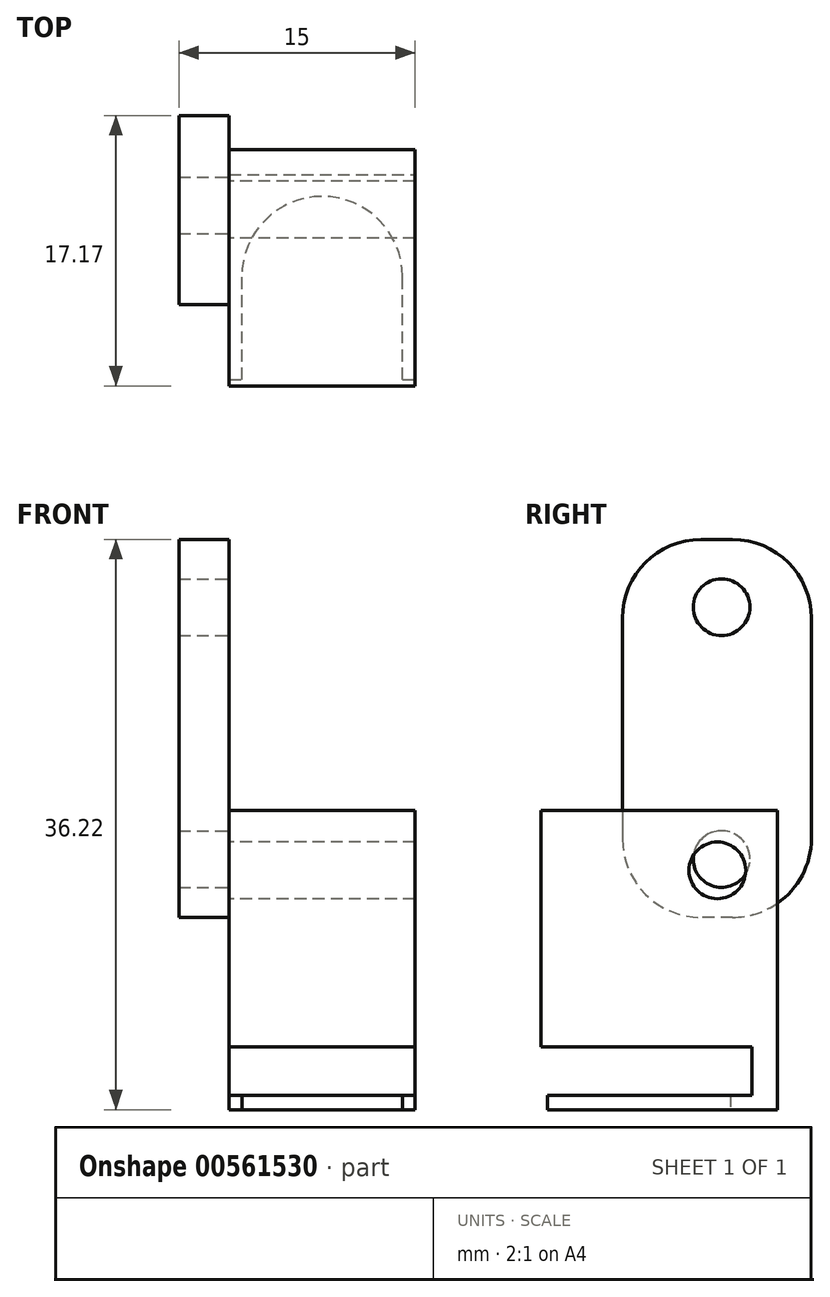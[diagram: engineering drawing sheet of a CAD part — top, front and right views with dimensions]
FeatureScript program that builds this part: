
annotation { "Feature Type Name" : "Feature", "Feature Type Description" : "" }
export const myFeature = defineFeature(function(context is Context, id is Id, definition is map)
    precondition{}
    {
        {
            var Q0;
            Q0=qCreatedBy(makeId("Front.planeOp"),FACE);
            var sketch = newSketch(context, id + "F0", { "sketchPlane" : qUnion([Q0])});
            skLineSegment(sketch, "E0.bottom", {"start": v(0, 15) * mm, "end": v(11.8, 15) * mm});
            skLineSegment(sketch, "E0.top", {"start": v(0, 0) * mm, "end": v(11.8, 0) * mm});
            skLineSegment(sketch, "E0.left", {"start": v(0, 15) * mm, "end": v(0, 0) * mm});
            skLineSegment(sketch, "E0.right", {"start": v(11.8, 15) * mm, "end": v(11.8, 0) * mm});
            skSolve(sketch);
        }
        {
            var Q0;
            Q0=makeQuery(id+"F0.imprint","IMPRINT",FACE,{"disambiguationData":[TD([[makeQuery(id+"F0.imprint","IMPRINT",EDGE,{"derivedFrom":sQuery(id+"F0.wireOp",EDGE,"E0.bottom")}),-1.0]])]});
            extrude(context, id + "F1", {"entities" : qUnion([Q0]), "depth" : 15 * mm, "offsetDistance" : 25 * mm});
        }
        {
            var Q0;
            Q0=makeQuery(id+"F1.opExtrude","SWEPT_FACE",FACE,{"disambiguationData":[OSD([sQuery(id+"F0.wireOp",EDGE,"E0.left")])]});
            var sketch = newSketch(context, id + "F2", { "sketchPlane" : qUnion([Q0])});
            skCircle(sketch, "E1", {"center": v(3.8, 11.2) * mm, "radius": 1.8 * mm});
            skSolve(sketch);
        }
        {
            var Q0;
            Q0=makeQuery(id+"F2.imprint","IMPRINT",FACE,{"disambiguationData":[TD([[makeQuery(id+"F2.imprint","IMPRINT",EDGE,{"derivedFrom":sQuery(id+"F2.wireOp",EDGE,"E1")}),1.0]])]});
            extrude(context, id + "F3", {"entities" : qUnion([Q0]), "operationType" : NewBodyOperationType.REMOVE, "oppositeDirection" : true, "depth" : 25 * mm, "offsetDistance" : 25 * mm});
        }
        {
            var Q0;
            Q0=makeQuery(id+"F1.opExtrude","SWEPT_FACE",FACE,{"disambiguationData":[OSD([sQuery(id+"F0.wireOp",EDGE,"E0.left")])]});
            var sketch = newSketch(context, id + "F4", { "sketchPlane" : qUnion([Q0])});
            skLineSegment(sketch, "E2.bottom", {"start": v(-2.17, 32.22) * mm, "end": v(9.83, 32.22) * mm});
            skLineSegment(sketch, "E2.top", {"start": v(-2.17, 8.22) * mm, "end": v(9.83, 8.22) * mm});
            skLineSegment(sketch, "E2.left", {"start": v(-2.17, 32.22) * mm, "end": v(-2.17, 8.22) * mm});
            skLineSegment(sketch, "E2.right", {"start": v(9.83, 32.22) * mm, "end": v(9.83, 8.22) * mm});
            skCircle(sketch, "E3", {"center": v(3.53, 27.92) * mm, "radius": 1.8 * mm});
            skCircle(sketch, "E4", {"center": v(3.53, 11.92) * mm, "radius": 1.8 * mm});
            skSolve(sketch);
        }
        {
            var Q0;
            Q0=qSketchRegion(id+"F4",true);
            extrude(context, id + "F5", {"entities" : qUnion([Q0]), "depth" : 3.2 * mm, "offsetDistance" : 25 * mm});
        }
        {
            var Q0;
            Q0=makeQuery(id+"F5.opExtrude","SWEPT_EDGE",EDGE,{"disambiguationData":[OSD([sQuery(id+"F4.wireOp",EDGE,"E2.bottom"),sQuery(id+"F4.wireOp",EDGE,"E2.left")])]});
            var Q1;
            Q1=makeQuery(id+"F5.opExtrude","SWEPT_EDGE",EDGE,{"disambiguationData":[OSD([sQuery(id+"F4.wireOp",EDGE,"E2.bottom"),sQuery(id+"F4.wireOp",EDGE,"E2.right")])]});
            var Q2;
            Q2=makeQuery(id+"F5.opExtrude","SWEPT_EDGE",EDGE,{"disambiguationData":[OSD([sQuery(id+"F4.wireOp",EDGE,"E2.top"),sQuery(id+"F4.wireOp",EDGE,"E2.right")])]});
            var Q3;
            Q3=makeQuery(id+"F5.opExtrude","SWEPT_EDGE",EDGE,{"disambiguationData":[OSD([sQuery(id+"F4.wireOp",EDGE,"E2.top"),sQuery(id+"F4.wireOp",EDGE,"E2.left")])]});
            fillet(context, id + "F6", {"entities" : qUnion([Q0, Q1, Q2, Q3]), "radius" : 5 * mm, "tangentPropagation" : true, "allowEdgeOverflow" : false});
        }
        {
            var Q0;
            Q0=makeQuery(id+"F1.opExtrude","SWEPT_FACE",FACE,{"disambiguationData":[OSD([sQuery(id+"F0.wireOp",EDGE,"E0.top")])]});
            var sketch = newSketch(context, id + "F7", { "sketchPlane" : qUnion([Q0])});
            skLineSegment(sketch, "E5", {"start": v(0, 1.59) * mm, "end": v(11.8, 1.59) * mm});
            skLineSegment(sketch, "E6", {"start": v(11.8, 1.59) * mm, "end": v(11.8, 0) * mm});
            skLineSegment(sketch, "E7", {"start": v(11.8, 0) * mm, "end": v(0, 0) * mm});
            skLineSegment(sketch, "E8", {"start": v(0, 0) * mm, "end": v(0, 1.59) * mm});
            skSolve(sketch);
        }
        {
            var Q0;
            Q0=qSketchRegion(id+"F7",true);
            extrude(context, id + "F8", {"entities" : qUnion([Q0]), "operationType" : NewBodyOperationType.ADD, "depth" : 4 * mm, "offsetDistance" : 25 * mm});
        }
        {
            var Q0;
            Q0=makeQuery(id+"F8.opExtrude","SWEPT_FACE",FACE,{"disambiguationData":[OSD([sQuery(id+"F7.wireOp",EDGE,"E5")])]});
            var sketch = newSketch(context, id + "F9", { "sketchPlane" : qUnion([Q0])});
            skLineSegment(sketch, "E9", {"start": v(0, -4) * mm, "end": v(0, -3.08) * mm});
            skLineSegment(sketch, "E10", {"start": v(0, -3.08) * mm, "end": v(11.8, -3.08) * mm});
            skLineSegment(sketch, "E11", {"start": v(11.8, -3.08) * mm, "end": v(11.8, -4) * mm});
            skLineSegment(sketch, "E12", {"start": v(11.8, -4) * mm, "end": v(0, -4) * mm});
            skSolve(sketch);
        }
        {
            var Q0;
            Q0=qSketchRegion(id+"F9",true);
            extrude(context, id + "F10", {"entities" : qUnion([Q0]), "operationType" : NewBodyOperationType.ADD, "depth" : 13 * mm, "offsetDistance" : 25 * mm});
        }
        {
            var Q0;
            Q0=makeQuery(id+"F10.boolean.opBoolean","MERGE",FACE,{"derivedFrom":[makeQuery(id+"F8.opExtrude","CAP_FACE",FACE,{"disambiguationData":[OSD([sQuery(id+"F7.wireOp",EDGE,"E5"),sQuery(id+"F7.wireOp",EDGE,"E6"),sQuery(id+"F7.wireOp",EDGE,"E7"),sQuery(id+"F7.wireOp",EDGE,"E8")])],"isStart":false}),makeQuery(id+"F10.opExtrude","SWEPT_FACE",FACE,{"disambiguationData":[OSD([sQuery(id+"F9.wireOp",EDGE,"E12")])]})]});
            var sketch = newSketch(context, id + "F11", { "sketchPlane" : qUnion([Q0])});
            skLineSegment(sketch, "E13", {"start": v(0.8, 14.59) * mm, "end": v(0.8, 8.06) * mm});
            skLineSegment(sketch, "E14", {"start": v(11, 14.59) * mm, "end": v(11, 8.06) * mm});
            skLineSegment(sketch, "E15", {"start": v(11, 14.59) * mm, "end": v(0.8, 14.59) * mm});
            skArc(sketch, "E16", {"start": v(0.8, 8.06) * mm, "mid": v(5.9, 2.96) * mm, "end": v(11, 8.06) * mm});
            skSolve(sketch);
        }
        {
            var Q0;
            Q0=qSketchRegion(id+"F11",true);
            extrude(context, id + "F12", {"entities" : qUnion([Q0]), "operationType" : NewBodyOperationType.REMOVE, "oppositeDirection" : true, "depth" : 2 * mm, "offsetDistance" : 25 * mm});
        }
    });
